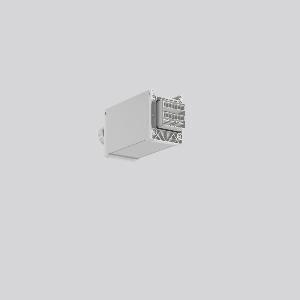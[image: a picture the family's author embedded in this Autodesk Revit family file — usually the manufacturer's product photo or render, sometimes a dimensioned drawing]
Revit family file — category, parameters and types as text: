
# Revit family: linedo_anfangseinspeisung_982859_000_1_4ad9
name_source: partatom
category: Lighting Fixtures
units: mm (PartAtom-declared; Revit-internal decimal feet)

## family parameters
Cut with Voids When Loaded = No
Host = Face
Light Source = No
Part Type = Normal
Room Calculation Point = No
Round Connector Dimension = Use Diameter
Shared = No

## types (1)
- LINEDO Anfangseinspeisung
    Apparent Load = 0 VA
    Default Elevation = 1800 mm
    Description = Series: LINEDO
Initial power feed (short Version), 7-pole, connection plug. Housing: extruded aluminium profile, anodised. Cover made of plastic, surface like housing. LINEDO plug system, plastic, light grey. 1 cable gland (M25). Cable gland on side or on top. Convenient connection with flat connector.
Colour: anodised aluminium
Length: 152 mm
Width: 58 mm
Height: 76 mm
Weight: 283 g
    Height = 76 mm
    Lamp = 0 x
    Length = 152 mm
    Luminous efficacy = 0 lm/W
    Manufacturer = RZB
    ModVariant = No
    Model = 982859.000.1
    Mounting Place = Ceiling
    Mounting Type = Surface mounted
    Number of Poles = 1
    OnlyDefault = Yes
    Power Factor = 1
    Product Name = LINEDO Anfangseinspeisung
    Product group = Surface mounted continuous line luminaire system
    ProductGroupID = 310
    Protection Class = Protection class I
    Protection Degree = Degree of protection
    RLX_Detail_Level = 1
    RLX_Emergency_Light_Flux = 0 lm
    RLX_Emergency_Type = 0
    RLX_Emergency_Type_DB = No
    RlxData = <blob elided: 13473 chars, md5=70771b2f>
    Standby Power = 0 W
    System Light Flux = 0 lm
    System Power = 0 W
    Type Comments = Product without accessories
    Type Image = 982859.000.1.jpg
    URL = http://relux.com
    VarID = ---
    Voltage = 0 V
    Weight = 0.00 kg
    Width = 58 mm

## geometry (parser evidence)
native form markers: Sweep x8
no freeform markers — native parametric forms only
